# Revit family: Detector de monóxido analógico direccionable_Aguilera Electronica
name_source: partatom
category: Dispositivos de alarma de incendios
revit_build: Autodesk Revit 2017 (Build: 20160225_1515(x64)
units: mm (PartAtom-declared; Revit-internal decimal feet)

## family parameters
Anfitrión = Cara
Compartido = No
Corte con vacíos al cargar = No
Cota de conector redondo = Diámetro de uso
Mantener orientación de anotación = Sí
Número OmniClass = 23.85.30.21.11.17
Punto de cálculo de habitación = No
Tipo de pieza = Normal
Título OmniClass = Other Components

## types (2) — shared parameters
Altura 1 = 20 mm  [stored 0.0656168 ft]
Altura 3 = 25 mm  [stored 0.082021 ft]
Descripción = Diseñado y fabricado por Aguilera Electrónica según normas UNE 23300-84 y homologados por el Ministerio de Industria y Energía.
Unidad microprocesada analógica direccionable indicada para detectar la presencia de monóxido de carbono.
Incorpora una sonda electroquímica.
Dimensiones 105 mm Ø x 55mm.
Diámetro tubo = 20 mm  [stored 0.0656168 ft]
Elevación por defecto = 1200 mm
Fabricante = Aguilera Electrónica
Símbolo = Sí
Símbolo texto modelo = Sí
URL = http://aguilera.es
Zona de acción = Sí

## per-type parameters (varying)
| type | Altura 2 | Comentarios de tipo | Diámetro | Modelo | Zócalo |
| Detector de monóxido analógico direccionable | 1 mm  [stored 0.00328084 ft] |  | 106 mm  [stored 0.347769 ft] | AE/COD | No |
| Detector de monóxido analógico direccionable con zócalo | 30 mm  [stored 0.0984252 ft] | Zócalo intercambiable que permite la entrada del tubo en instalaciones vistas. | 105 mm  [stored 0.344488 ft] | AE/COD + AE/ZCO | Sí |

note: [stored X ft] marks values corroborated as IEEE doubles in the binary element streams (Revit-internal decimal feet)
